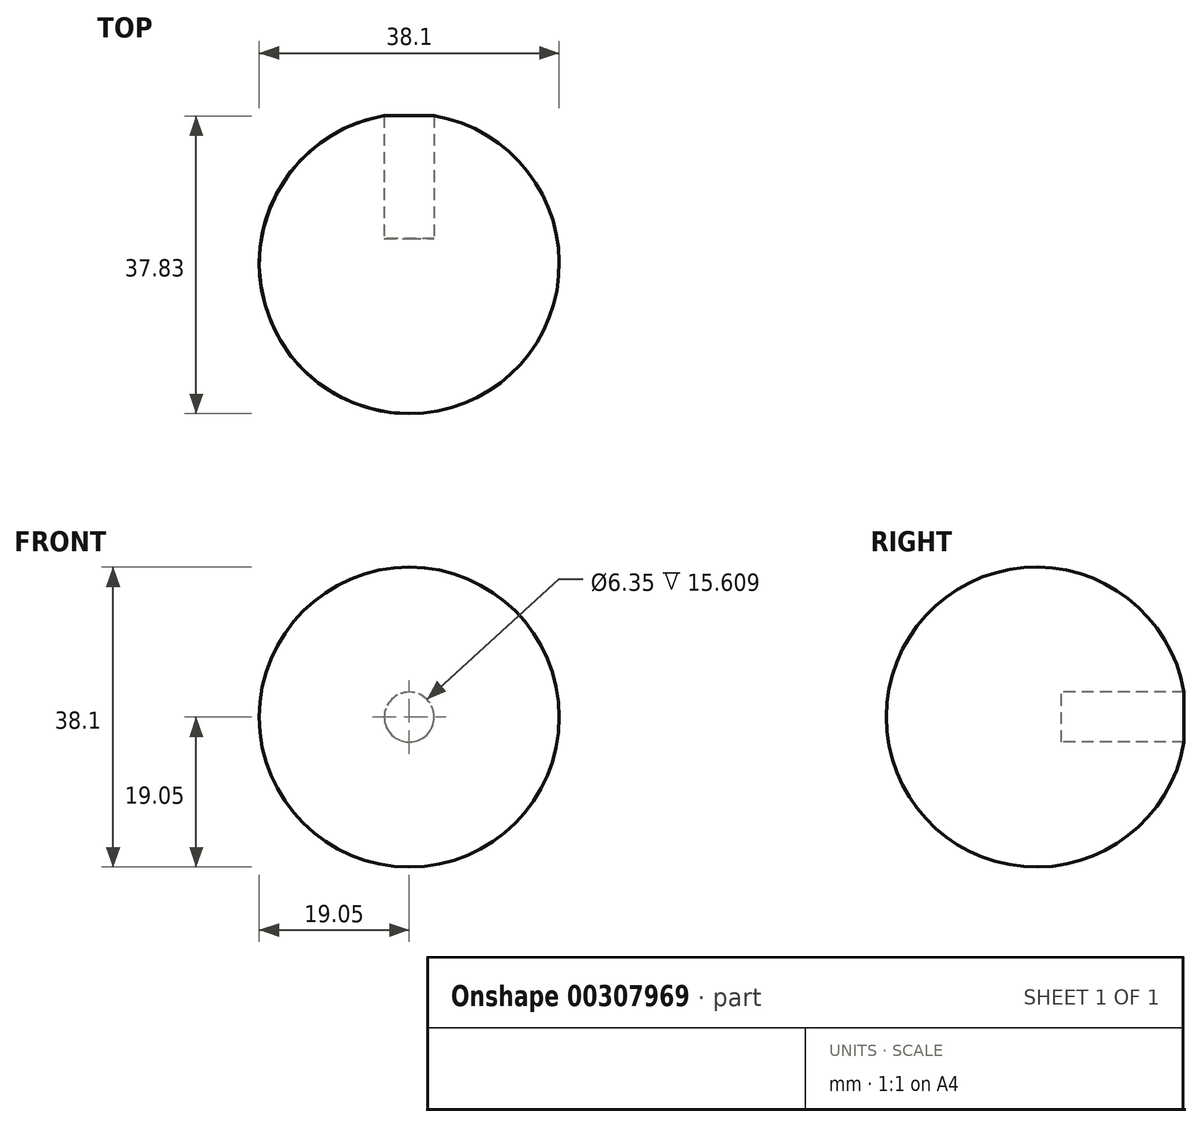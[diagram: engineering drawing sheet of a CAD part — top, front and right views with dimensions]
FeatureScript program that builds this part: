
annotation { "Feature Type Name" : "Feature", "Feature Type Description" : "" }
export const myFeature = defineFeature(function(context is Context, id is Id, definition is map)
    precondition{}
    {
        {
            var Q0;
            Q0=qCreatedBy(makeId("Front.planeOp"),FACE);
            var sketch = newSketch(context, id + "F0", { "sketchPlane" : qUnion([Q0])});
            skCircle(sketch, "E0", {"center": v(0, 0) * mm, "radius": 19.05 * mm});
            skSolve(sketch);
        }
        {
            var Q0;
            Q0=qCreatedBy(makeId("Top.planeOp"),FACE);
            var sketch = newSketch(context, id + "F1", { "sketchPlane" : qUnion([Q0])});
            skArc(sketch, "E1", {"start": v(0, 19.05) * mm, "mid": v(-19.05, 0) * mm, "end": v(0, -19.05) * mm});
            skLineSegment(sketch, "E2", {"start": v(0, -19.05) * mm, "end": v(0, 19.05) * mm});
            skSolve(sketch);
        }
        {
            var Q0;
            Q0=makeQuery(id+"F1.imprint","IMPRINT",FACE,{"disambiguationData":[TD([[makeQuery(id+"F1.imprint","IMPRINT",EDGE,{"derivedFrom":sQuery(id+"F1.wireOp",EDGE,"E1")}),1.0]])]});
            var Q1;
            Q1=sQuery(id+"F0.wireOp",EDGE,"E0");
            revolve(context, id + "F2", {"entities" : qUnion([Q0]), "axis" : qUnion([Q1]), "revolveType" : RevolveType.FULL});
        }
        {
            var Q0;
            Q0=qCreatedBy(makeId("Front.planeOp"),FACE);
            cPlane(context, id + "F3", {"entities" : qUnion([Q0]), "cplaneType" : CPlaneType.OFFSET, "offset" : 3.17 * mm, "oppositeDirection" : true, "width" : 152.4 * mm, "height" : 152.4 * mm});
        }
        {
            var Q0;
            Q0=qCreatedBy(id+"F3.planeOp",FACE);
            var sketch = newSketch(context, id + "F4", { "sketchPlane" : qUnion([Q0])});
            skCircle(sketch, "E3", {"center": v(0, 0) * mm, "radius": 3.18 * mm});
            skSolve(sketch);
        }
        {
            var Q0;
            Q0 = qSketchRegion(id + "F4", true);
            extrude(context, id + "F5", {"entities" : qUnion([Q0]), "oppositeDirection" : true, "depth" : 76.2 * mm});
        }
        {
            var Q0;
            Q0=makeQuery(id+"F5.opExtrude","SWEPT_BODY",BODY,{"disambiguationData":[OSD([sQuery(id+"F4.wireOp",EDGE,"E3")])]});
            var Q1;
            Q1=makeQuery(id+"F2.opRevolve","SWEPT_BODY",BODY,{"disambiguationData":[OSD([sQuery(id+"F1.wireOp",EDGE,"E1"),sQuery(id+"F1.wireOp",EDGE,"E2")])]});
            booleanBodies(context, id + "F6", {"operationType" : BooleanOperationType.SUBTRACTION, "tools" : qUnion([Q0]), "targets" : qUnion([Q1])});
        }
    });
